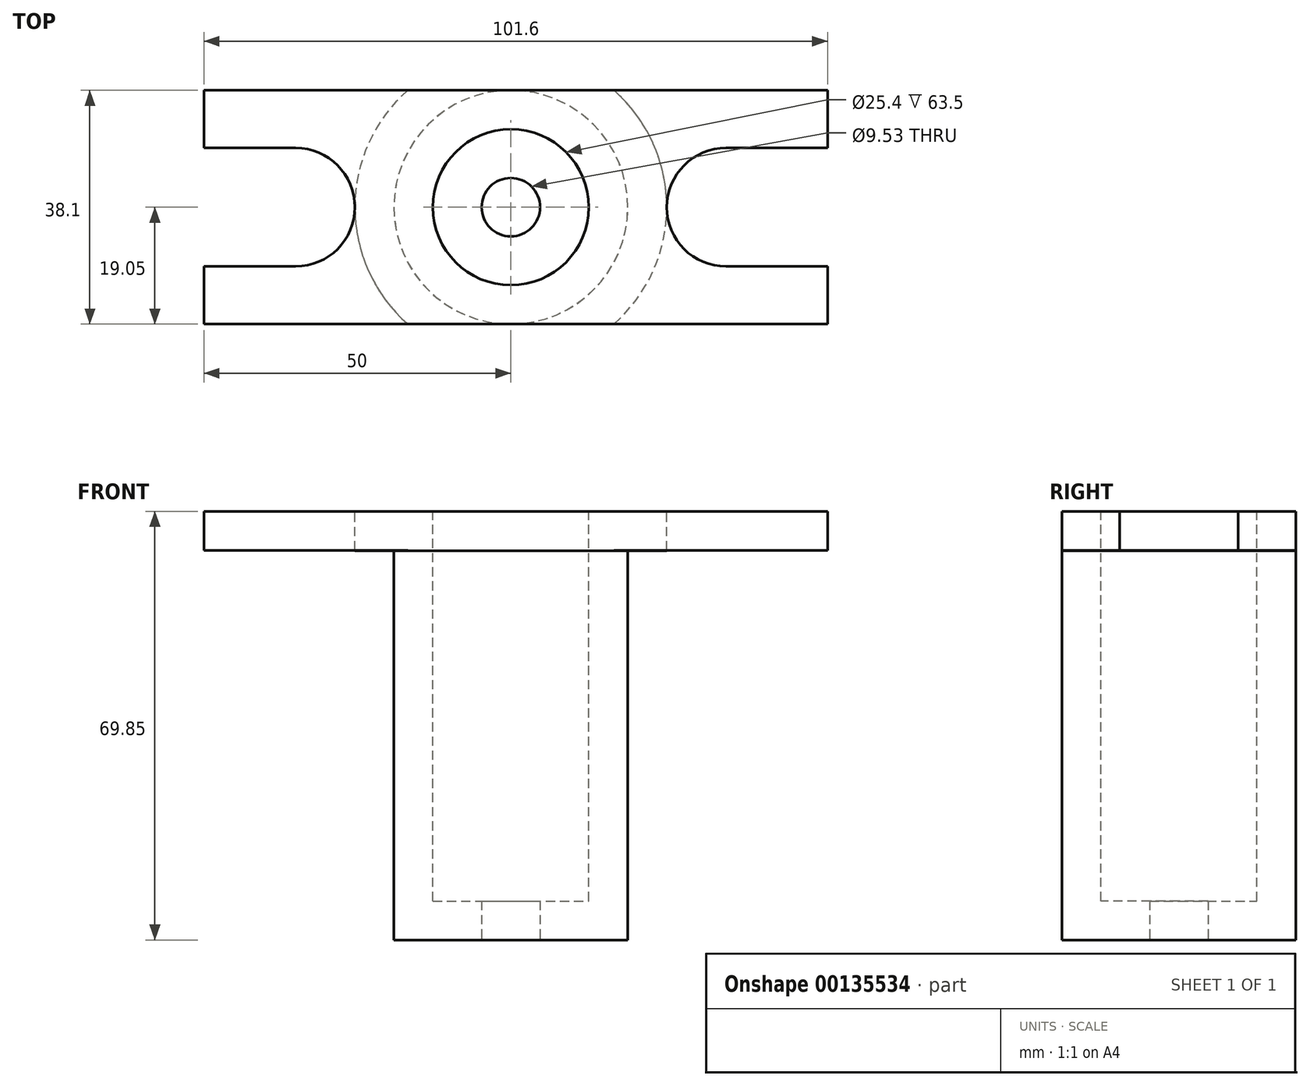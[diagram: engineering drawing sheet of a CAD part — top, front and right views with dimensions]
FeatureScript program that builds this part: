
annotation { "Feature Type Name" : "Feature", "Feature Type Description" : "" }
export const myFeature = defineFeature(function(context is Context, id is Id, definition is map)
    precondition{}
    {
        {
            var Q0;
            Q0=qCreatedBy(makeId("Front.planeOp"),FACE);
            var sketch = newSketch(context, id + "F0", { "sketchPlane" : qUnion([Q0])});
            skLineSegment(sketch, "E0", {"start": v(0, 0) * mm, "end": v(12.7, 0) * mm});
            skLineSegment(sketch, "E1", {"start": v(12.7, 0) * mm, "end": v(12.7, -63.5) * mm});
            skLineSegment(sketch, "E2", {"start": v(12.7, -63.5) * mm, "end": v(4.76, -63.5) * mm});
            skLineSegment(sketch, "E3", {"start": v(4.76, -63.5) * mm, "end": v(4.76, -69.85) * mm});
            skLineSegment(sketch, "E4", {"start": v(12.7, 0) * mm, "end": v(25.4, 0) * mm});
            skLineSegment(sketch, "E5", {"start": v(25.4, 0) * mm, "end": v(25.4, -6.44) * mm});
            skLineSegment(sketch, "E6", {"start": v(25.4, -6.44) * mm, "end": v(19.05, -6.44) * mm});
            skPoint(sketch, "E6.endSnap0", {"position": v(19.05, 0) * mm});
            skLineSegment(sketch, "E7", {"start": v(19.05, -6.44) * mm, "end": v(19.05, -69.85) * mm});
            skLineSegment(sketch, "E8", {"start": v(19.05, -69.85) * mm, "end": v(4.76, -69.85) * mm});
            skLineSegment(sketch, "E9", {"start": v(0, -73.86) * mm, "end": v(0, 43.52) * mm, "construction": true});
            skSolve(sketch);
        }
        {
            var Q0;
            Q0=makeQuery(id+"F0.imprint","IMPRINT",FACE,{"disambiguationData":[TD([[makeQuery(id+"F0.imprint","IMPRINT",EDGE,{"derivedFrom":sQuery(id+"F0.wireOp",EDGE,"E1")}),1.0]])]});
            var Q1;
            Q1=sQuery(id+"F0.wireOp",EDGE,"E9");
            revolve(context, id + "F1", {"entities" : qUnion([Q0]), "axis" : qUnion([Q1]), "revolveType" : RevolveType.FULL});
        }
        {
            var Q0;
            Q0=qCreatedBy(makeId("Front.planeOp"),FACE);
            var sketch = newSketch(context, id + "F2", { "sketchPlane" : qUnion([Q0])});
            skLineSegment(sketch, "E10", {"start": v(0, 0) * mm, "end": v(51.6, 0) * mm});
            skLineSegment(sketch, "E11", {"start": v(51.6, 0) * mm, "end": v(51.6, -6.35) * mm});
            skLineSegment(sketch, "E12", {"start": v(51.6, -6.35) * mm, "end": v(0, -6.35) * mm});
            skLineSegment(sketch, "E13", {"start": v(0, -6.35) * mm, "end": v(-50, -6.35) * mm});
            skLineSegment(sketch, "E14", {"start": v(-50, -6.35) * mm, "end": v(-50, 0) * mm});
            skLineSegment(sketch, "E15", {"start": v(-50, 0) * mm, "end": v(0, 0) * mm});
            skSolve(sketch);
        }
        {
            var Q0;
            Q0 = qSketchRegion(id + "F2", true);
            extrude(context, id + "F3", {"entities" : qUnion([Q0]), "depth" : 19.05 * mm, "hasSecondDirection" : true, "secondDirectionOppositeDirection" : true, "secondDirectionDepth" : 19.05 * mm});
        }
        {
            var Q0;
            Q0=qCreatedBy(makeId("Top.planeOp"),FACE);
            var sketch = newSketch(context, id + "F4", { "sketchPlane" : qUnion([Q0])});
            skCircle(sketch, "E16", {"center": v(0, 0) * mm, "radius": 12.7 * mm});
            skSolve(sketch);
        }
        {
            var Q0;
            Q0 = qSketchRegion(id + "F4", true);
            extrude(context, id + "F5", {"entities" : qUnion([Q0]), "operationType" : NewBodyOperationType.REMOVE, "oppositeDirection" : true, "depth" : 25.4 * mm});
        }
        {
            var Q0;
            Q0=makeQuery(id+"F3.opExtrude","SWEPT_BODY",BODY,{"disambiguationData":[OSD([sQuery(id+"F2.wireOp",EDGE,"E10"),sQuery(id+"F2.wireOp",EDGE,"E11"),sQuery(id+"F2.wireOp",EDGE,"E12"),sQuery(id+"F2.wireOp",EDGE,"E13"),sQuery(id+"F2.wireOp",EDGE,"E14"),sQuery(id+"F2.wireOp",EDGE,"E15")])]});
            var Q1;
            Q1=makeQuery(id+"F1.opRevolve","SWEPT_BODY",BODY,{"disambiguationData":[OSD([sQuery(id+"F0.wireOp",EDGE,"E1"),sQuery(id+"F0.wireOp",EDGE,"E2"),sQuery(id+"F0.wireOp",EDGE,"E3"),sQuery(id+"F0.wireOp",EDGE,"E4"),sQuery(id+"F0.wireOp",EDGE,"E5"),sQuery(id+"F0.wireOp",EDGE,"E6"),sQuery(id+"F0.wireOp",EDGE,"E7"),sQuery(id+"F0.wireOp",EDGE,"E8")])]});
            booleanBodies(context, id + "F6", {"operationType" : BooleanOperationType.UNION, "tools" : qUnion([Q0, Q1])});
        }
        {
            var Q0;
            Q0=qCreatedBy(makeId("Top.planeOp"),FACE);
            var sketch = newSketch(context, id + "F7", { "sketchPlane" : qUnion([Q0])});
            skLineSegment(sketch, "E17", {"start": v(0, 27.2) * mm, "end": v(58.3, 27.2) * mm, "construction": true});
            skLineSegment(sketch, "E18", {"start": v(58.3, 27.2) * mm, "end": v(58.3, -39.6) * mm, "construction": true});
            skLineSegment(sketch, "E19", {"start": v(58.3, -39.6) * mm, "end": v(-53.45, -39.6) * mm, "construction": true});
            skLineSegment(sketch, "E20", {"start": v(-53.45, -39.6) * mm, "end": v(-53.45, 27.2) * mm, "construction": true});
            skLineSegment(sketch, "E21", {"start": v(-53.45, 27.2) * mm, "end": v(0, 27.2) * mm, "construction": true});
            skLineSegment(sketch, "E22", {"start": v(0, 0) * mm, "end": v(35.05, 0) * mm});
            skLineSegment(sketch, "E23", {"start": v(0, 19.05) * mm, "end": v(-16.8, 19.05) * mm});
            skLineSegment(sketch, "E24", {"start": v(0, 19.05) * mm, "end": v(16.8, 19.05) * mm});
            skLineSegment(sketch, "E25", {"start": v(0, -19.05) * mm, "end": v(16.8, -19.05) * mm});
            skLineSegment(sketch, "E26", {"start": v(0, -19.05) * mm, "end": v(-16.8, -19.05) * mm});
            skLineSegment(sketch, "E27", {"start": v(-16.8, 19.05) * mm, "end": v(-16.8, 27.2) * mm});
            skLineSegment(sketch, "E28", {"start": v(-16.8, 27.2) * mm, "end": v(16.8, 27.2) * mm});
            skLineSegment(sketch, "E29", {"start": v(16.8, 27.2) * mm, "end": v(16.8, 19.05) * mm});
            skLineSegment(sketch, "E30", {"start": v(-16.8, -19.05) * mm, "end": v(-16.8, -29.42) * mm});
            skLineSegment(sketch, "E31", {"start": v(-16.8, -29.42) * mm, "end": v(16.8, -29.42) * mm});
            skLineSegment(sketch, "E32", {"start": v(16.8, -29.42) * mm, "end": v(16.8, -19.05) * mm});
            skArc(sketch, "E33", {"start": v(25.4, 0) * mm, "mid": v(28.23, -6.82) * mm, "end": v(35.05, -9.65) * mm});
            skLineSegment(sketch, "E34", {"start": v(35.05, -9.65) * mm, "end": v(51.6, -9.65) * mm});
            skLineSegment(sketch, "E35", {"start": v(51.6, -9.65) * mm, "end": v(51.6, -19.05) * mm});
            skArc(sketch, "E36", {"start": v(35.05, -9.65) * mm, "mid": v(25.4, 0) * mm, "end": v(35.05, 9.65) * mm});
            skLineSegment(sketch, "E37", {"start": v(35.05, 9.65) * mm, "end": v(51.6, 9.65) * mm});
            skLineSegment(sketch, "E38", {"start": v(51.6, 9.65) * mm, "end": v(51.6, 19.05) * mm});
            skLineSegment(sketch, "E39", {"start": v(51.6, 19.05) * mm, "end": v(-50, 19.05) * mm});
            skLineSegment(sketch, "E40", {"start": v(51.6, -19.05) * mm, "end": v(-50, -19.05) * mm});
            skArc(sketch, "E41", {"start": v(-35.05, -9.65) * mm, "mid": v(-25.4, 0) * mm, "end": v(-35.05, 9.65) * mm});
            skLineSegment(sketch, "E42", {"start": v(-35.05, 9.65) * mm, "end": v(-50, 9.65) * mm});
            skLineSegment(sketch, "E43", {"start": v(-50, 9.65) * mm, "end": v(-50, 19.05) * mm});
            skLineSegment(sketch, "E44", {"start": v(-35.05, -9.65) * mm, "end": v(-50, -9.65) * mm});
            skLineSegment(sketch, "E45", {"start": v(-50, -9.65) * mm, "end": v(-50, -19.05) * mm});
            skLineSegment(sketch, "E46", {"start": v(51.6, -9.65) * mm, "end": v(51.6, 9.65) * mm});
            skLineSegment(sketch, "E47", {"start": v(-50, -9.65) * mm, "end": v(-50, 9.65) * mm});
            skSolve(sketch);
        }
        {
            var Q0;
            {var subQ3=sQuery(id+"F7.wireOp",EDGE,"E30");Q0=makeQuery(id+"F7.imprint","IMPRINT",FACE,{"disambiguationData":[TD([[makeQuery(id+"F7.imprint","IMPRINT",EDGE,{"derivedFrom":subQ3}),1.0]])]});}
            var Q1;
            {var subQ3=sQuery(id+"F7.wireOp",EDGE,"E27");Q1=makeQuery(id+"F7.imprint","IMPRINT",FACE,{"disambiguationData":[TD([[makeQuery(id+"F7.imprint","IMPRINT",EDGE,{"derivedFrom":subQ3}),-1.0]])]});}
            extrude(context, id + "F8", {"entities" : qUnion([Q0, Q1]), "operationType" : NewBodyOperationType.REMOVE, "endBound" : BoundingType.THROUGH_ALL, "oppositeDirection" : true, "depth" : 25.4 * mm});
        }
        {
            var Q0;
            {var subQ2=sQuery(id+"F7.wireOp",EDGE,"E34");Q0=makeQuery(id+"F7.imprint","IMPRINT",FACE,{"disambiguationData":[TD([[makeQuery(id+"F7.imprint","IMPRINT",EDGE,{"derivedFrom":subQ2}),1.0]])]});}
            var Q1;
            Q1=makeQuery(id+"F7.imprint","IMPRINT",FACE,{"disambiguationData":[TD([[makeQuery(id+"F7.imprint","IMPRINT",EDGE,{"derivedFrom":sQuery(id+"F7.wireOp",EDGE,"E41")}),1.0]])]});
            extrude(context, id + "F9", {"entities" : qUnion([Q0, Q1]), "operationType" : NewBodyOperationType.REMOVE, "oppositeDirection" : true, "depth" : 25.4 * mm});
        }
    });
